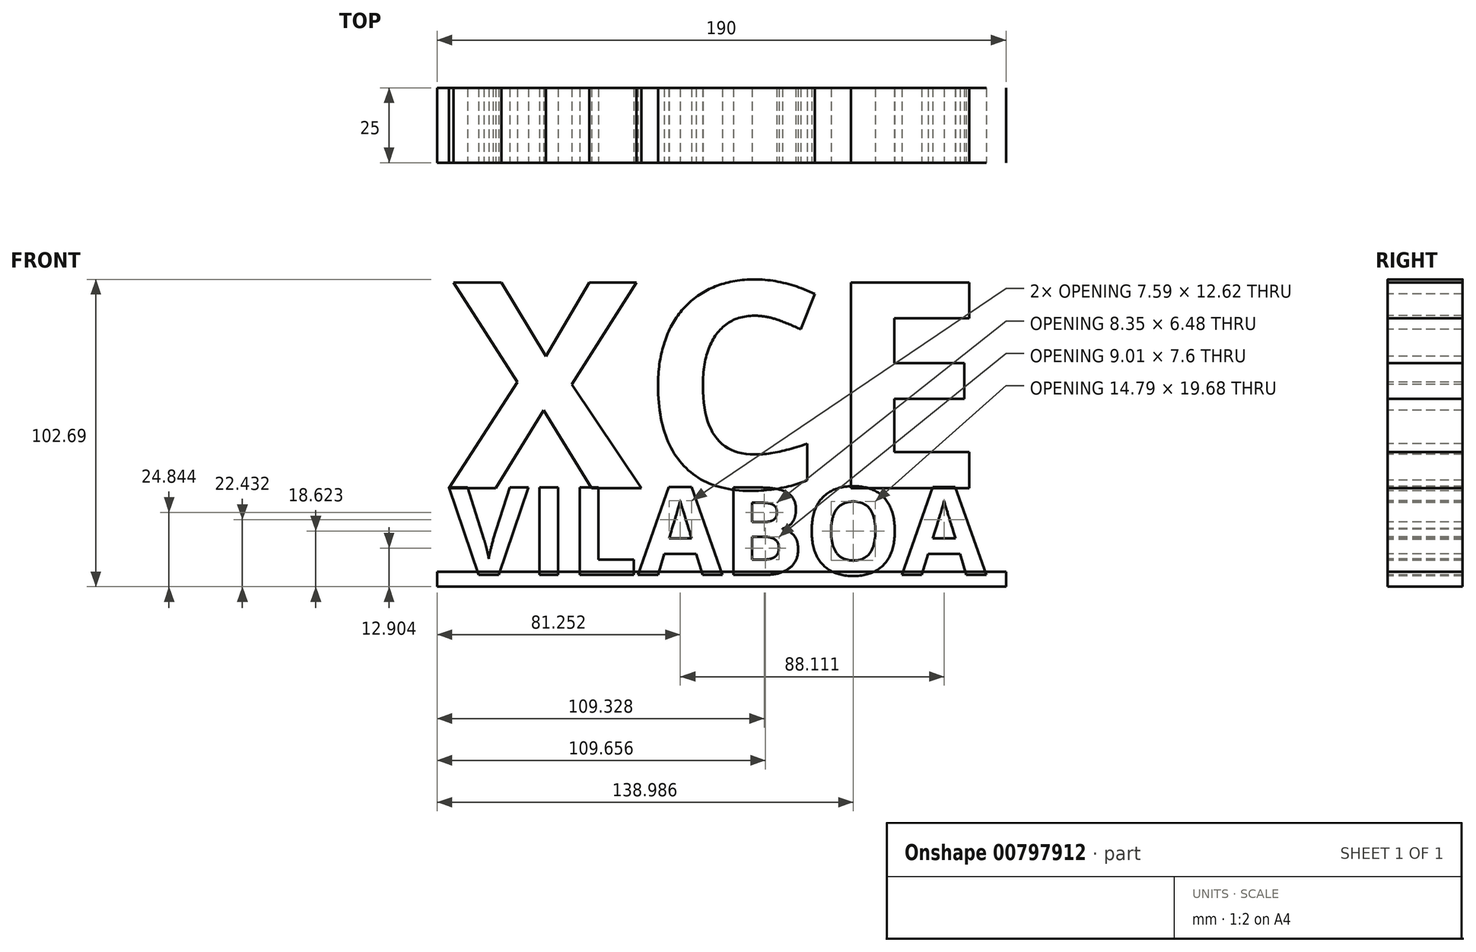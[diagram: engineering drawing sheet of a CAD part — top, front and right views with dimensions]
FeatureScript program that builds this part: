
annotation { "Feature Type Name" : "Feature", "Feature Type Description" : "" }
export const myFeature = defineFeature(function(context is Context, id is Id, definition is map)
    precondition{}
    {
        {
            var Q0;
            Q0=qCreatedBy(makeId("Top.planeOp"),FACE);
            var sketch = newSketch(context, id + "F0", { "sketchPlane" : qUnion([Q0])});
            skLineSegment(sketch, "E0", {"start": v(-95, -37.63) * mm, "end": v(95, -37.63) * mm});
            skLineSegment(sketch, "E1", {"start": v(-95, -37.63) * mm, "end": v(-95, -12.63) * mm});
            skLineSegment(sketch, "E2", {"start": v(-95, -12.63) * mm, "end": v(95, -12.63) * mm});
            skLineSegment(sketch, "E3", {"start": v(95, -37.63) * mm, "end": v(95, -12.63) * mm});
            skSolve(sketch);
        }
        {
            var Q0;
            Q0 = qSketchRegion(id + "F0", true);
            extrude(context, id + "F1", {"entities" : qUnion([Q0]), "depth" : 5 * mm, "offsetDistance" : 25 * mm});
        }
        {
            var Q0;
            Q0=makeQuery(id+"F1.opExtrude","SWEPT_FACE",FACE,{"disambiguationData":[OSD([sQuery(id+"F0.wireOp",EDGE,"E0")])]});
            var sketch = newSketch(context, id + "F2", { "sketchPlane" : qUnion([Q0])});
            skText(sketch, "E4", { "text": "VILABOA", "fontName": "OpenSans-Bold.ttf"});
            const initialGuessF2  = {"E4": [-0.091, 0.004, 1, 0, 0.0294]};
            skSetInitialGuess(sketch, initialGuessF2);
            skSolve(sketch);
        }
        {
            var Q0;
            Q0 = qSketchRegion(id + "F2", true);
            extrude(context, id + "F3", {"entities" : qUnion([Q0]), "oppositeDirection" : true, "depth" : 25 * mm, "offsetDistance" : 25 * mm});
        }
        {
            var Q0;
            Q0=makeQuery(id+"F3.opExtrude","CAP_FACE",FACE,{"disambiguationData":[OSD([sQuery(id+"F2.wireOp",EDGE,"E4.sketch_text.stroke-0"),sQuery(id+"F2.wireOp",EDGE,"E4.sketch_text.stroke-1"),sQuery(id+"F2.wireOp",EDGE,"E4.sketch_text.stroke-2"),sQuery(id+"F2.wireOp",EDGE,"E4.sketch_text.stroke-3"),sQuery(id+"F2.wireOp",EDGE,"E4.sketch_text.stroke-4"),sQuery(id+"F2.wireOp",EDGE,"E4.sketch_text.stroke-5"),sQuery(id+"F2.wireOp",EDGE,"E4.sketch_text.stroke-6"),sQuery(id+"F2.wireOp",EDGE,"E4.sketch_text.stroke-7"),sQuery(id+"F2.wireOp",EDGE,"E4.sketch_text.stroke-8"),sQuery(id+"F2.wireOp",EDGE,"E4.sketch_text.stroke-9")])],"isStart":true});
            var sketch = newSketch(context, id + "F4", { "sketchPlane" : qUnion([Q0])});
            skText(sketch, "E5", { "text": "XCE", "fontName": "OpenSans-Bold.ttf"});
            const initialGuessF4  = {"E5": [-0.091, 0.033, 1, 0, 0.0693]};
            skSetInitialGuess(sketch, initialGuessF4);
            skSolve(sketch);
        }
        {
            var Q0;
            Q0 = qSketchRegion(id + "F4", true);
            extrude(context, id + "F5", {"entities" : qUnion([Q0]), "oppositeDirection" : true, "depth" : 25 * mm, "offsetDistance" : 25 * mm});
        }
    });
